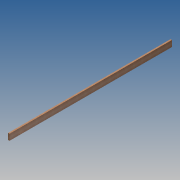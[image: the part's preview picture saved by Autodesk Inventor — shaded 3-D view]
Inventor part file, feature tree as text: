
AUTODESK INVENTOR PART (.ipt)
format: ipt  version: 2013 (Build 170138000, 138)  size: 69,632 bytes
history: native  units: in
note: dims shown in document units (in); Inventor stores cm internally (conversion verified against a paired STEP export)
features: extrude x1, sketch x1
ambient origin geometry x8: Origin, YZ Plane, XZ Plane, XY Plane, X Axis, Y Axis, Z Axis, Center Point
bodies: Solid1 (feature_tree)
feature tree (2):
  extrude  "Extrusion1"  Depth=7.5in
  sketch  "Sketch1"  dims[d0=1.75in d1=7.5in d2=200.0in d3=0.0in]
